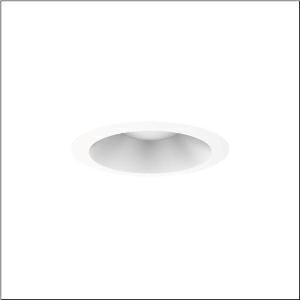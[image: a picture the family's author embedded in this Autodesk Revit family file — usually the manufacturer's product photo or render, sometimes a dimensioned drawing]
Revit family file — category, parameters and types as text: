
# Revit family: lunis_31_midi_51dn157g42
name_source: partatom
category: Lighting Fixtures
units: mm (PartAtom-declared; Revit-internal decimal feet)

## family parameters
Cut with Voids When Loaded = No
Host = Face
Light Source = No
Part Type = Normal
Room Calculation Point = No
Round Connector Dimension = Use Diameter
Shared = No

## types (1)
- Lunis 31 midi (1 x LED, 2150 lm, 17 W, 4000K)
    Apparent Load = 17 VA
    CIE Flux Codes = 89 99 100 100 100
    Color Rendering = 80
    Color Temperature = 4000K
    Default Elevation = 1800 mm
    Description = Lunis 31,  midi, downlight, light control with lens, light emission: direct distribution, LED rated luminous flux: 2.150lm, light colour: 840, mains connection: 220..240V, AC, 50/60Hz, housing, white, protection rating (complete): IP20, protection rating (on room side): IP54, insulation class (complete): insulation class II (safety insulation), certification: CE, packaging unit: 1 piece
    Height = 0 mm  [stored 0 ft]
    Lamp = 1 x LED
    Lamp Light Flux = 2150 lm
    Lamp Power = 17 W
    Lamp count = 1
    Length = 259 mm
    Luminous efficacy = 126 lm/W
    Manufacturer = Siteco
    ModVariant = No
    Model = 51DN157G42
    Mounting Place = Ceiling
    Mounting Type = Recessed
    Number of Poles = 1
    OnlyDefault = Yes
    Power Factor = 1
    Product Name = Lunis 31 midi
    Product group = downlight
    ProductGroupID = 400
    Protection Class = Protection class II
    Protection Degree = IP 20
    RLX_Detail_Level = 1
    RLX_Emergency_Light_Flux = 0 lm
    RLX_Emergency_Type = 0
    RLX_Emergency_Type_DB = No
    RlxData = <blob elided: 23745 chars, md5=42a43dda>
    Socket = socket
    Standby Power = 0 W
    System Light Flux = 2150 lm
    System Power = 17 W
    Type Comments = Product without accessories
    Type Image = l_1006711.jpg
    URL = http://relux.com
    VarID = ---
    Voltage = 0 V
    Weight = 0.00 kg
    Width = 0 mm  [stored 0 ft]

note: [stored X ft] marks values corroborated as IEEE doubles in the binary element streams (Revit-internal decimal feet)

## geometry (parser evidence)
native form markers: Blend x4, Sweep x13
no freeform markers — native parametric forms only
